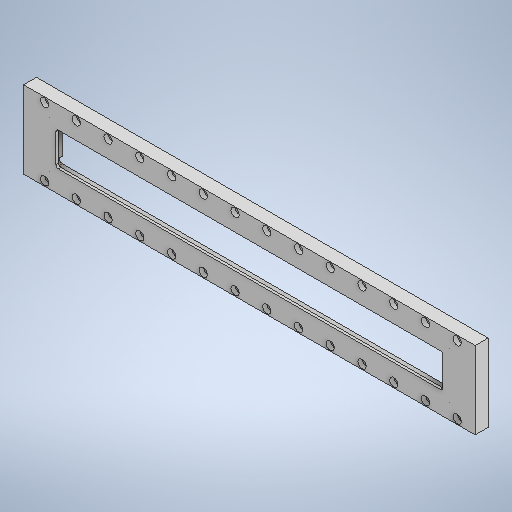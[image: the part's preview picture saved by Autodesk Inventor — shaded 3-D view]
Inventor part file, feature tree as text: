
AUTODESK INVENTOR PART (.ipt)
format: ipt  version: 2025.2 (Build 292293000, 293)  size: 374,272 bytes
history: native  units: mm
features: fillet x4, other x4, sketch x4, extrude x3, hole x1, pattern_linear x1
ambient origin geometry x8: Origin, YZ Plane, XZ Plane, XY Plane, X Axis, Y Axis, Z Axis, Center Point
bodies: Volumenkörper1 (feature_tree)
feature tree (17):
  extrude  "Extrusion1"  TaperAngle=0.0deg  [1 undecoded]
  extrude  "Extrusion2"  Depth=10.0mm TaperAngle=0.0deg
  fillet  "Rundung1"  Radius=25.0mm
  fillet  "Rundung2"  Radius=25.0mm
  fillet  "Rundung3"  Radius=17.0mm
  fillet  "Rundung4"  Radius=17.0mm
  extrude  "Extrusion4"  Depth=2.0mm
  other  "Arbeitsachse1"
  other  "Arbeitsachse2"
  other  "Arbeitsachse3"
  other  "Arbeitsachse4"
  hole  "Bohrung8"  [1 undecoded]
  pattern_linear  "Rechteckige Anordnung2"  Spacing1=2.0mm  [1 undecoded]
  sketch  "Skizze1"  dims[d0=350.0mm d1=0.0mm]
  sketch  "Skizze2"  dims[d2=60.0mm d3=10.0mm d4=0.0mm d5=25.0mm d6=25.0mm d7=17.0mm d8=17.0mm]
  sketch  "Skizze4"  dims[d9=0.0mm d10=0.0mm d11=2.0mm]
  sketch  "Skizze14"  dims[d12=2.0mm d13=2.0mm d14=2.0mm d32=5.0mm d33=5.0mm d35=8.0mm d36=0.0mm d110=2.5mm d111=2.5mm d112=2.5mm d113=2.5mm d114=5.0mm d115=5.0mm d116=3.75mm d117=16.3mm d118=3.4mm d119=6.0mm d120=6.5mm d121=3.4mm d122=90.0deg d123=8.0mm d124=20.594885mm d125=140.0mm d127=24.6mm d128=20.0mm d130=52.5mm d91=1.0mm d92=1.0mm d93=1.0mm d94=0.15mm d95=0.25mm d96=0.375mm d97=14.3117mm d98=0.75mm d99=20.594885mm d100=0.0625mm d101=0.75mm d102=0.375mm]
note: 3 required parameter values undecoded (feature->parameter linkage not recoverable at this tier; creation-order binding heuristic only, values carry confidence <= 0.55)
